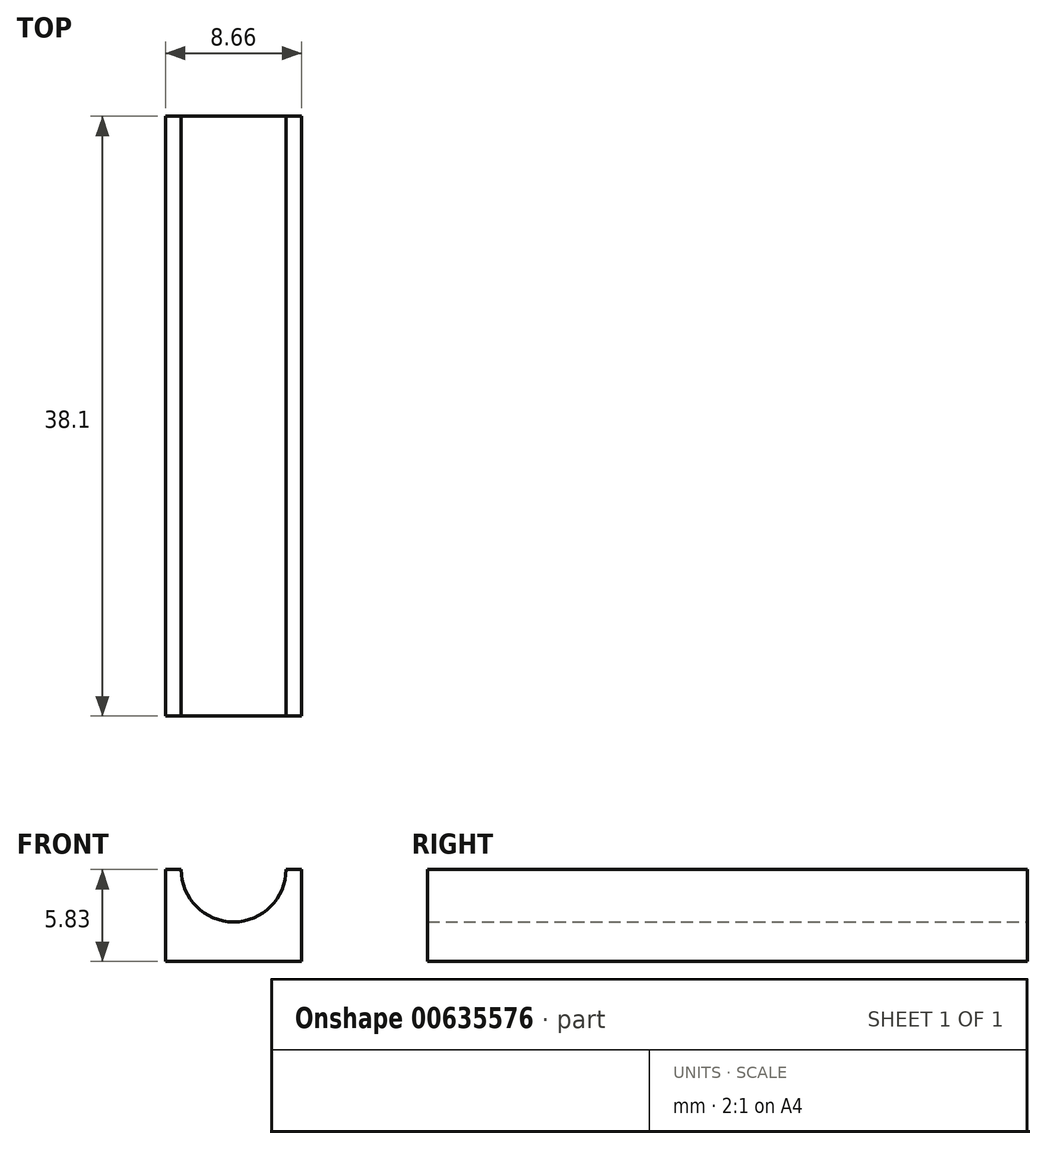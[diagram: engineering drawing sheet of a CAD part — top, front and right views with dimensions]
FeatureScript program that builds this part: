
annotation { "Feature Type Name" : "Feature", "Feature Type Description" : "" }
export const myFeature = defineFeature(function(context is Context, id is Id, definition is map)
    precondition{}
    {
        {
            var Q0;
            Q0=qCreatedBy(makeId("Front.planeOp"),FACE);
            var sketch = newSketch(context, id + "F0", { "sketchPlane" : qUnion([Q0])});
            skCircle(sketch, "E0", {"center": v(0, 0) * mm, "radius": 3.18 * mm, "construction": true});
            skLineSegment(sketch, "E1.bottom", {"start": v(-4.33, 0) * mm, "end": v(4.33, 0) * mm});
            skLineSegment(sketch, "E1.top", {"start": v(-4.33, -5.83) * mm, "end": v(4.33, -5.83) * mm});
            skLineSegment(sketch, "E1.left", {"start": v(-4.33, 0) * mm, "end": v(-4.33, -5.83) * mm});
            skLineSegment(sketch, "E1.right", {"start": v(4.33, 0) * mm, "end": v(4.33, -5.83) * mm});
            skPoint(sketch, "E1.middle", {"position": v(0, -2.92) * mm});
            skCircle(sketch, "E2", {"center": v(0, 0) * mm, "radius": 3.33 * mm});
            skSolve(sketch);
        }
        {
            var Q0;
            Q0=makeQuery(id+"F0.imprint","IMPRINT",FACE,{"disambiguationData":[TD([[makeQuery(id+"F0.imprint","IMPRINT",EDGE,{"derivedFrom":sQuery(id+"F0.wireOp",EDGE,"E1.top")}),1.0]])]});
            extrude(context, id + "F1", {"entities" : qUnion([Q0]), "endBound" : BoundingType.SYMMETRIC, "depth" : 38.1 * mm, "offsetDistance" : 25.4 * mm});
        }
    });
